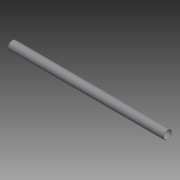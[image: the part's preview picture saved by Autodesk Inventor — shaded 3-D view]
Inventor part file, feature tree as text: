
AUTODESK INVENTOR PART (.ipt)
format: ipt  version: 2014 SP2 (Build 180246200, 246)  size: 116,224 bytes
history: native  units: in
note: dims shown in document units (in); Inventor stores cm internally (conversion verified against a paired STEP export)
features: other x42, revolve x1, sketch x1
ambient origin geometry x8: Origin, YZ Plane, XZ Plane, XY Plane, X Axis, Y Axis, Z Axis, Center Point
bodies: Solid1 (feature_tree)
feature tree (44):
  revolve  "Revolution1"  [1 undecoded]
  other  "cp1_XY"
  other  "cp1_YZ"
  other  "cp1_ZX"
  other  "cp1_X"
  other  "cp1_Y"
  other  "cp1_Z"
  other  "cp1_Center"
  other  "cp2_XY"
  other  "cp2_YZ"
  other  "cp2_ZX"
  other  "cp2_X"
  other  "cp2_Y"
  other  "cp2_Z"
  other  "cp2_Center"
  other  "cp3_XY"
  other  "cp3_YZ"
  other  "cp3_ZX"
  other  "cp3_X"
  other  "cp3_Y"
  other  "cp3_Z"
  other  "cp3_Center"
  other  "cp4_XY"
  other  "cp4_YZ"
  other  "cp4_ZX"
  other  "cp4_X"
  other  "cp4_Y"
  other  "cp4_Z"
  other  "cp4_Center"
  other  "tube_front_XY"
  other  "tube_front_YZ"
  other  "tube_front_ZX"
  other  "tube_front_X"
  other  "tube_front_Y"
  other  "tube_front_Z"
  other  "tube_front_Center"
  other  "tube_rear_XY"
  other  "tube_rear_YZ"
  other  "tube_rear_ZX"
  other  "tube_rear_X"
  other  "tube_rear_Y"
  other  "tube_rear_Z"
  other  "tube_rear_Center"
  sketch  "Sketch_1"  dims[d0=360.0deg]
note: 1 required parameter value undecoded (feature->parameter linkage not recoverable at this tier; creation-order binding heuristic only, values carry confidence <= 0.55)
